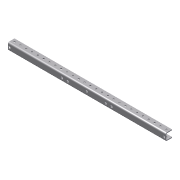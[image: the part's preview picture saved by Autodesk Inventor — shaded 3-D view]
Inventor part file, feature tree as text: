
AUTODESK INVENTOR PART (.ipt)
format: ipt  version: 2013 (Build 170138000, 138)  size: 216,576 bytes
history: native  units: in
note: dims shown in document units (in); Inventor stores cm internally (conversion verified against a paired STEP export)
features: projected_geometry x8, extrude x2, sketch x2, other x1, imported_body x1
ambient origin geometry x8: Origin, YZ Plane, XZ Plane, XY Plane, X Axis, Y Axis, Z Axis, Center Point
feature tree (14):
  other  "Short C Channel for drive1"
  extrude  "Extrusion1"  TaperAngle=0.0deg  [1 undecoded]
  extrude  "Extrusion2"  [1 undecoded]
  imported_body  "Base1"
  sketch  "Sketch1"  dims[d1=0.0in d3=0.0in]
  projected_geometry  "Projected Loop1"
  projected_geometry  "Projected Loop2"
  projected_geometry  "Projected Loop3"
  projected_geometry  "Projected Loop4"
  sketch  "Sketch2"
  projected_geometry  "Projected Loop5"
  projected_geometry  "Projected Loop6"
  projected_geometry  "Projected Loop7"
  projected_geometry  "Projected Loop8"
note: 2 required parameter values undecoded (feature->parameter linkage not recoverable at this tier; creation-order binding heuristic only, values carry confidence <= 0.55)
